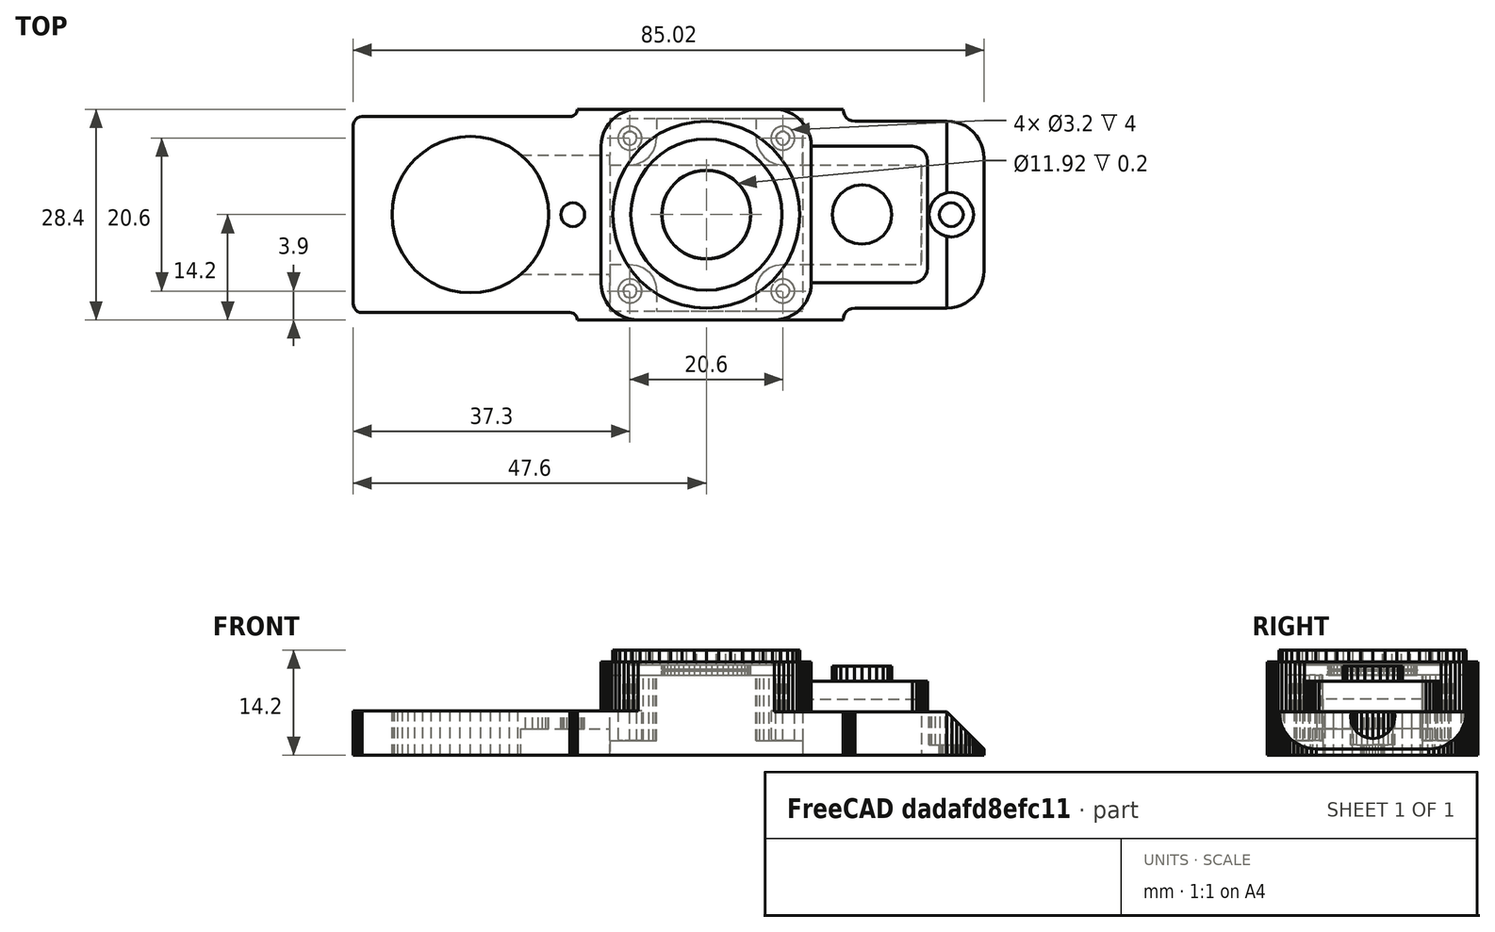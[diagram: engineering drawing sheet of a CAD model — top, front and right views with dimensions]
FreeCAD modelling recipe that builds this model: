
FCSTD DOCUMENT  (FreeCAD 1.0R39319 (Git))
Label: frontale_analogico_corretto
License: All rights reserved
LicenseURL: https://en.wikipedia.org/wiki/All_rights_reserved
objects: Part::Cylinder×5, PartDesign::Body×1, Part::Feature×1, Part::Scale×1, Part::MultiFuse×1, Part::Cut×1
note: 10 computed .brp shape members not serialized (recipe doc carries the construction recipe); baked Part::Feature solids carry a one-line shape summary decoded from their .brp

FEATURE [PartDesign::Body] Body  label="Corpo"
  AllowCompound = false
  Origin = -> Origin
FEATURE [Part::Feature] Part__Feature  label="originale_anteriore"
  shape: bbox 850.2 x 284 x 142 mm, 2681 faces (baked)
FEATURE [Part::Scale] Scale
  Base = -> Part__Feature
  Uniform = true
  UniformScale = 0.1
  XScale = 1
  YScale = 1
  ZScale = 1
FEATURE [Part::Cylinder] Cylinder001  label="buco principale"
  Angle = 360
  AttacherType = Attacher::AttachEngine3D
  FirstAngle = 0
  Height = 10
  Placement = pos=(5.09,9.99,5) rot=(0,0,1;0rad)
  Radius = 5.96
  SecondAngle = 0
FEATURE [Part::Cylinder] Cylinder002  label="-x-y"
  Angle = 360
  AttacherType = Attacher::AttachEngine3D
  FirstAngle = 0
  Height = 6
  Placement = pos=(-5.21,-0.31,0) rot=(0,0,1;0rad)
  Radius = 1.6
  SecondAngle = 0
FEATURE [Part::Cylinder] Cylinder003  label="+x-y"
  Angle = 360
  AttacherType = Attacher::AttachEngine3D
  FirstAngle = 0
  Height = 6
  Placement = pos=(-5.21,20.29,0) rot=(0,0,1;0rad)
  Radius = 1.6
  SecondAngle = 0
FEATURE [Part::Cylinder] Cylinder004  label="-x+y"
  Angle = 360
  AttacherType = Attacher::AttachEngine3D
  FirstAngle = 0
  Height = 6
  Placement = pos=(15.39,-0.31,0) rot=(0,0,1;0rad)
  Radius = 1.6
  SecondAngle = 0
FEATURE [Part::Cylinder] Cylinder005  label="+x+y"
  Angle = 360
  AttacherType = Attacher::AttachEngine3D
  FirstAngle = 0
  Height = 6
  Placement = pos=(15.39,20.29,0) rot=(0,0,1;0rad)
  Radius = 1.6
  SecondAngle = 0
FEATURE [Part::MultiFuse] Fusion
  Refine = true
  Shapes = -> [Cylinder001,Cylinder002,Cylinder003,Cylinder004,Cylinder005]
FEATURE [Part::Cut] Cut
  Base = -> Scale
  Refine = true
  Tool = -> Fusion
